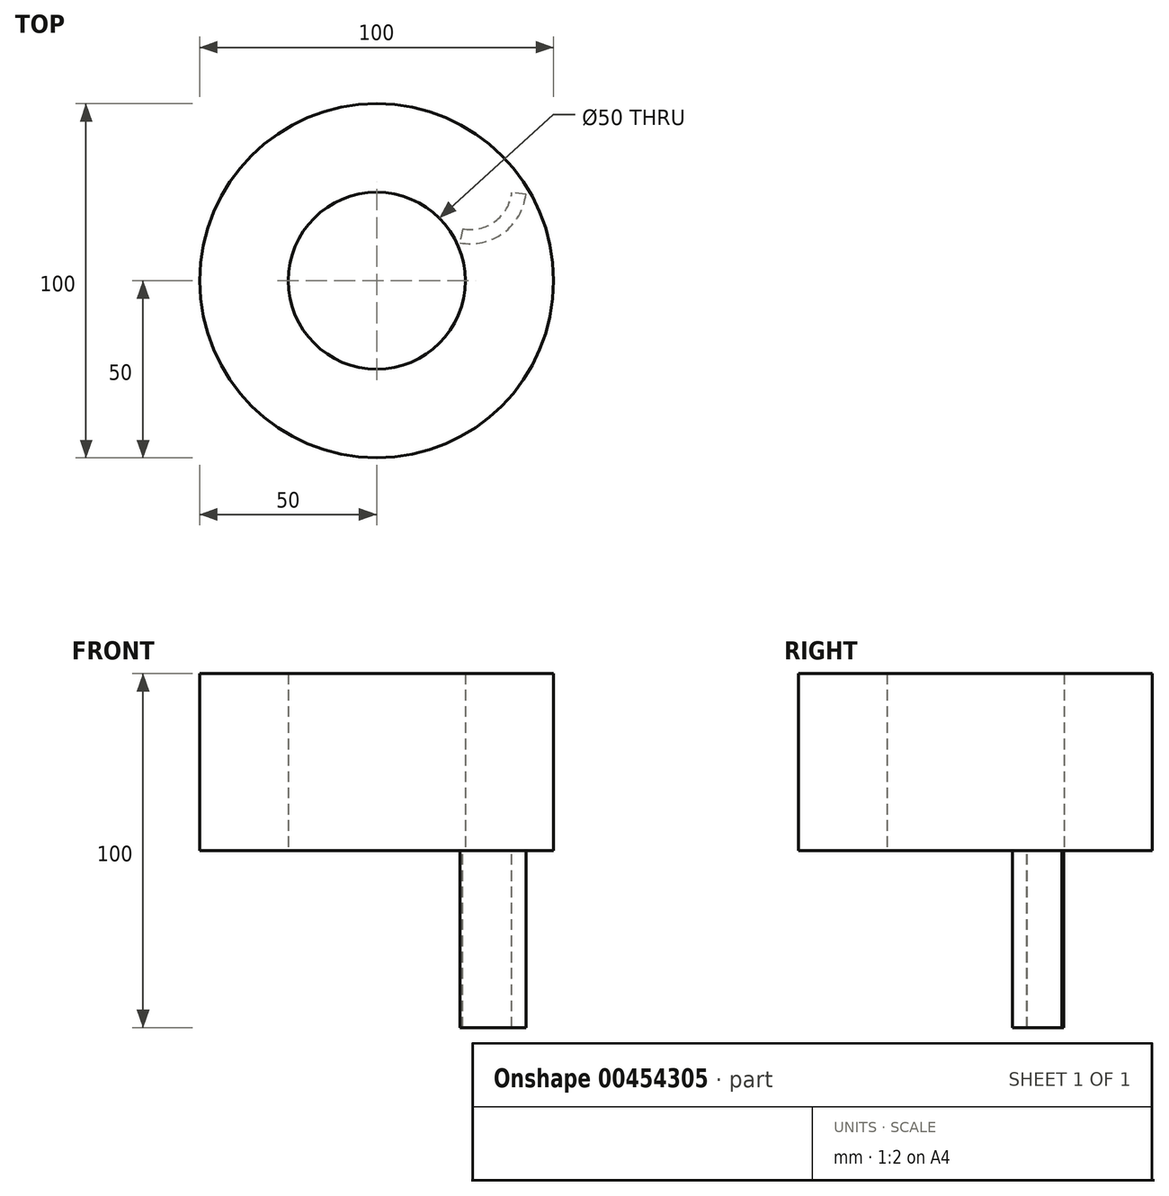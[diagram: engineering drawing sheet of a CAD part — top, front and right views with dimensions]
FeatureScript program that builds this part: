
annotation { "Feature Type Name" : "Feature", "Feature Type Description" : "" }
export const myFeature = defineFeature(function(context is Context, id is Id, definition is map)
    precondition{}
    {
        {
            var Q0;
            Q0=qCreatedBy(makeId("Top.planeOp"),FACE);
            var sketch = newSketch(context, id + "F0", { "sketchPlane" : qUnion([Q0])});
            skCircle(sketch, "E0", {"center": v(0, 0) * mm, "radius": 50 * mm});
            skSolve(sketch);
        }
        {
            var Q0;
            Q0 = qSketchRegion(id + "F0", true);
            extrude(context, id + "F1", {"entities" : qUnion([Q0]), "depth" : 50 * mm});
        }
        {
            var Q0;
            Q0=qCreatedBy(makeId("Top.planeOp"),FACE);
            var sketch = newSketch(context, id + "F2", { "sketchPlane" : qUnion([Q0])});
            skCircle(sketch, "E1", {"center": v(0, 0) * mm, "radius": 25 * mm});
            skSolve(sketch);
        }
        {
            var Q0;
            Q0 = qSketchRegion(id + "F2", true);
            extrude(context, id + "F3", {"entities" : qUnion([Q0]), "operationType" : NewBodyOperationType.REMOVE, "depth" : 50 * mm});
        }
        {
            var Q0;
            Q0=qCreatedBy(makeId("Top.planeOp"),FACE);
            var sketch = newSketch(context, id + "F4", { "sketchPlane" : qUnion([Q0])});
            skArc(sketch, "E2", {"start": v(23.48, 10.75) * mm, "mid": v(35.8, 13.53) * mm, "end": v(42.15, 24.43) * mm});
            skArc(sketch, "E3.0", {"start": v(24.24, 14.68) * mm, "mid": v(33.43, 16.75) * mm, "end": v(38.17, 24.9) * mm});
            skLineSegment(sketch, "E4", {"start": v(42.15, 24.43) * mm, "end": v(38.17, 24.9) * mm});
            skLineSegment(sketch, "E5", {"start": v(24.24, 14.68) * mm, "end": v(23.48, 10.75) * mm});
            skSolve(sketch);
        }
        {
            var Q0;
            Q0 = qSketchRegion(id + "F4", true);
            extrude(context, id + "F5", {"entities" : qUnion([Q0]), "operationType" : NewBodyOperationType.ADD, "oppositeDirection" : true, "depth" : 50 * mm});
        }
    });
